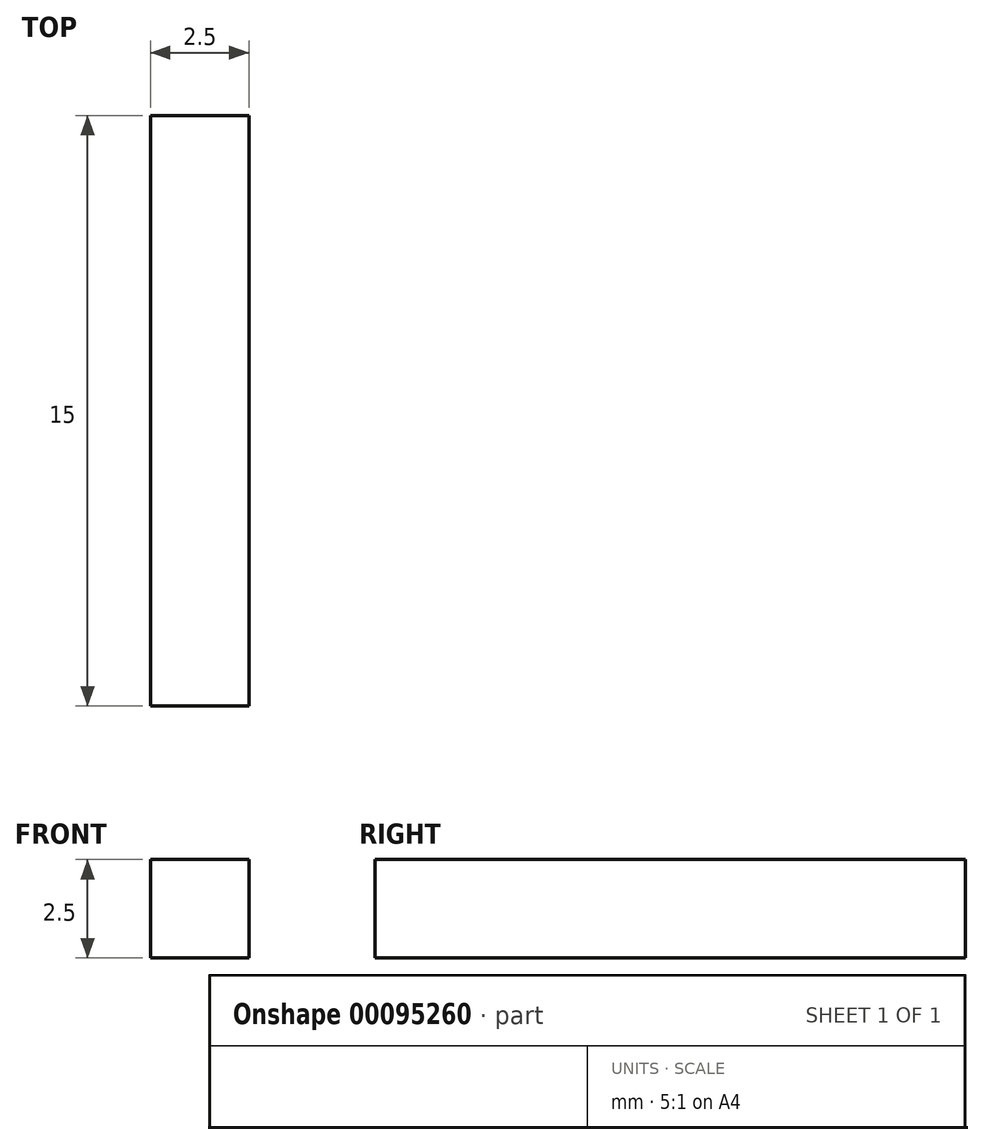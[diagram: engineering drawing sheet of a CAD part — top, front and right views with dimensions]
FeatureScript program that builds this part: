
annotation { "Feature Type Name" : "Feature", "Feature Type Description" : "" }
export const myFeature = defineFeature(function(context is Context, id is Id, definition is map)
    precondition{}
    {
        {
            var Q0;
            Q0=qCreatedBy(makeId("Front.planeOp"),FACE);
            var sketch = newSketch(context, id + "F0", { "sketchPlane" : qUnion([Q0])});
            skLineSegment(sketch, "E0.bottom", {"start": v(1.25, 1.25) * mm, "end": v(-1.25, 1.25) * mm});
            skLineSegment(sketch, "E0.top", {"start": v(1.25, -1.25) * mm, "end": v(-1.25, -1.25) * mm});
            skLineSegment(sketch, "E0.left", {"start": v(1.25, 1.25) * mm, "end": v(1.25, -1.25) * mm});
            skLineSegment(sketch, "E0.right", {"start": v(-1.25, 1.25) * mm, "end": v(-1.25, -1.25) * mm});
            skPoint(sketch, "E0.middle", {"position": v(0, 0) * mm});
            skSolve(sketch);
        }
        {
            var Q0;
            Q0 = qSketchRegion(id + "F0", true);
            extrude(context, id + "F1", {"entities" : qUnion([Q0]), "depth" : 15 * mm});
        }
    });
